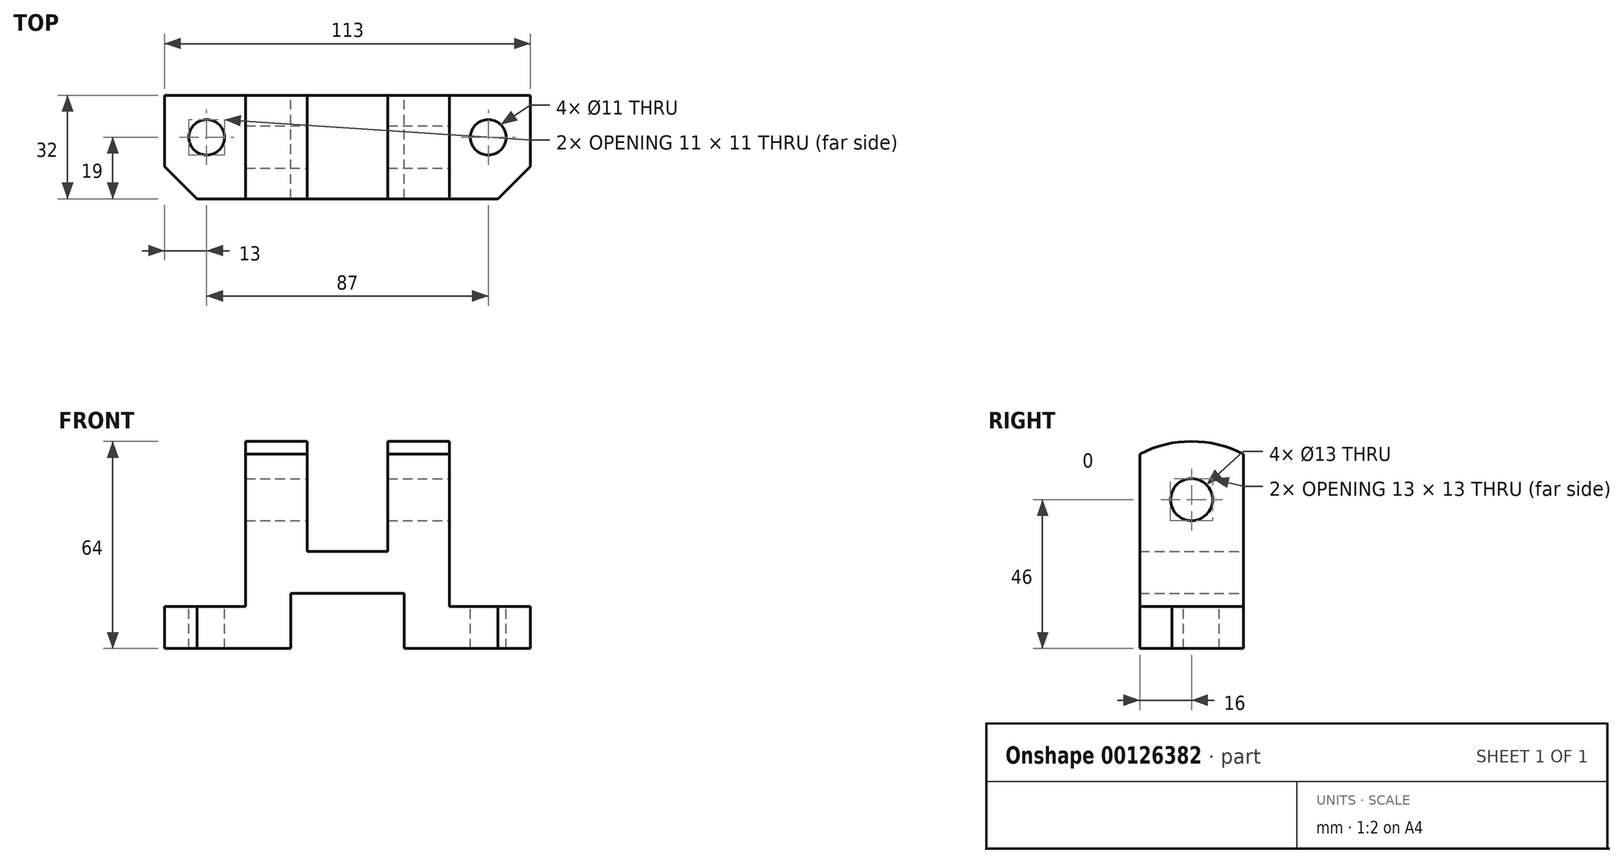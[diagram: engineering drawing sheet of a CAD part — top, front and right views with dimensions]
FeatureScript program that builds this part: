
annotation { "Feature Type Name" : "Feature", "Feature Type Description" : "" }
export const myFeature = defineFeature(function(context is Context, id is Id, definition is map)
    precondition{}
    {
        {
            var Q0;
            Q0=qCreatedBy(makeId("Front.planeOp"),FACE);
            var sketch = newSketch(context, id + "F0", { "sketchPlane" : qUnion([Q0])});
            skLineSegment(sketch, "E0", {"start": v(0, 0) * mm, "end": v(0, 13) * mm});
            skLineSegment(sketch, "E1", {"start": v(0, 13) * mm, "end": v(25, 13) * mm});
            skLineSegment(sketch, "E2", {"start": v(25, 13) * mm, "end": v(25, 64) * mm});
            skLineSegment(sketch, "E3", {"start": v(25, 64) * mm, "end": v(44, 64) * mm});
            skLineSegment(sketch, "E4", {"start": v(44, 64) * mm, "end": v(44, 30) * mm});
            skLineSegment(sketch, "E5", {"start": v(44, 30) * mm, "end": v(69, 30) * mm});
            skLineSegment(sketch, "E6", {"start": v(69, 30) * mm, "end": v(69, 64) * mm});
            skLineSegment(sketch, "E7", {"start": v(69, 64) * mm, "end": v(88, 64) * mm});
            skLineSegment(sketch, "E8", {"start": v(88, 64) * mm, "end": v(88, 13) * mm});
            skLineSegment(sketch, "E9", {"start": v(88, 13) * mm, "end": v(113, 13) * mm});
            skLineSegment(sketch, "E10", {"start": v(113, 13) * mm, "end": v(113, 0) * mm});
            skLineSegment(sketch, "E11", {"start": v(113, 0) * mm, "end": v(74, 0) * mm});
            skLineSegment(sketch, "E12", {"start": v(74, 0) * mm, "end": v(74, 17) * mm});
            skLineSegment(sketch, "E13", {"start": v(74, 17) * mm, "end": v(39, 17) * mm});
            skLineSegment(sketch, "E14", {"start": v(39, 17) * mm, "end": v(39, 0) * mm});
            skLineSegment(sketch, "E15", {"start": v(39, 0) * mm, "end": v(0, 0) * mm});
            skSolve(sketch);
        }
        {
            var Q0;
            Q0=makeQuery(id+"F0.imprint","IMPRINT",FACE,{"disambiguationData":[TD([[makeQuery(id+"F0.imprint","IMPRINT",EDGE,{"derivedFrom":sQuery(id+"F0.wireOp",EDGE,"E0")}),-1.0]])]});
            extrude(context, id + "F1", {"entities" : qUnion([Q0]), "endBound" : BoundingType.SYMMETRIC, "depth" : 32 * mm});
        }
        {
            var Q0;
            Q0=makeQuery(id+"F1.opExtrude","SWEPT_FACE",FACE,{"disambiguationData":[OSD([sQuery(id+"F0.wireOp",EDGE,"E8")])]});
            var sketch = newSketch(context, id + "F2", { "sketchPlane" : qUnion([Q0])});
            skLineSegment(sketch, "E16.0", {"start": v(-16, 64) * mm, "end": v(-16, 13) * mm});
            skLineSegment(sketch, "E16.1", {"start": v(16, 64) * mm, "end": v(16, 13) * mm});
            skArc(sketch, "E17", {"start": v(16, 60.13) * mm, "mid": v(0, 64) * mm, "end": v(-16, 60.13) * mm});
            skLineSegment(sketch, "E18.0", {"start": v(-16, 64) * mm, "end": v(16, 64) * mm});
            skCircle(sketch, "E19", {"center": v(0, 46) * mm, "radius": 6.5 * mm});
            skLineSegment(sketch, "E20", {"start": v(0, -19.5) * mm, "end": v(0, 83.55) * mm, "construction": true});
            skSolve(sketch);
        }
        {
            var Q0;
            Q0=makeQuery(id+"F2.imprint","IMPRINT",FACE,{"disambiguationData":[TD([[makeQuery(id+"F2.imprint","IMPRINT",EDGE,{"derivedFrom":sQuery(id+"F2.wireOp",EDGE,"E19")}),1.0]])]});
            extrude(context, id + "F3", {"entities" : qUnion([Q0]), "operationType" : NewBodyOperationType.REMOVE, "endBound" : BoundingType.THROUGH_ALL, "oppositeDirection" : true, "depth" : 25 * mm});
        }
        {
            var Q0;
            {var subQ0=sQuery(id+"F2.wireOp",EDGE,"E18.0");var subQ1=sQuery(id+"F2.wireOp",EDGE,"E16.1");var subQ2=makeQuery(id+"F2.imprint","INTERSECT",VERTEX,{"derivedFrom":[subQ1,subQ0]});Q0=makeQuery(id+"F2.imprint","IMPRINT",FACE,{"disambiguationData":[TD([[makeQuery(id+"F2.imprint","IMPRINT",EDGE,{"disambiguationData":[TD([[subQ2,-1.0]])],"derivedFrom":subQ1}),-1.0]])]});}
            var Q1;
            {var subQ0=sQuery(id+"F2.wireOp",EDGE,"E18.0");var subQ1=sQuery(id+"F2.wireOp",EDGE,"E16.0");var subQ2=makeQuery(id+"F2.imprint","INTERSECT",VERTEX,{"derivedFrom":[subQ1,subQ0]});Q1=makeQuery(id+"F2.imprint","IMPRINT",FACE,{"disambiguationData":[TD([[makeQuery(id+"F2.imprint","IMPRINT",EDGE,{"disambiguationData":[TD([[subQ2,-1.0]])],"derivedFrom":subQ1}),1.0]])]});}
            extrude(context, id + "F4", {"entities" : qUnion([Q0, Q1]), "operationType" : NewBodyOperationType.REMOVE, "endBound" : BoundingType.THROUGH_ALL, "oppositeDirection" : true, "depth" : 25 * mm});
        }
        {
            var Q0;
            Q0=makeQuery(id+"F1.opExtrude","SWEPT_FACE",FACE,{"disambiguationData":[OSD([sQuery(id+"F0.wireOp",EDGE,"E9")])]});
            var sketch = newSketch(context, id + "F5", { "sketchPlane" : qUnion([Q0])});
            skLineSegment(sketch, "E21.0", {"start": v(88, -16) * mm, "end": v(113, -16) * mm});
            skLineSegment(sketch, "E21.1", {"start": v(113, -16) * mm, "end": v(113, 16) * mm});
            skLineSegment(sketch, "E22", {"start": v(103, -16) * mm, "end": v(113, -6) * mm});
            skCircle(sketch, "E23", {"center": v(100, 3) * mm, "radius": 5.5 * mm});
            skLineSegment(sketch, "E24", {"start": v(103, -16) * mm, "end": v(113, -16) * mm});
            skLineSegment(sketch, "E25", {"start": v(113, -16) * mm, "end": v(113, -6) * mm});
            skSolve(sketch);
        }
        {
            var Q0;
            Q0=makeQuery(id+"F5.imprint","IMPRINT",FACE,{"disambiguationData":[TD([[makeQuery(id+"F5.imprint","IMPRINT",EDGE,{"derivedFrom":sQuery(id+"F5.wireOp",EDGE,"E23")}),1.0]])]});
            extrude(context, id + "F6", {"entities" : qUnion([Q0]), "operationType" : NewBodyOperationType.REMOVE, "endBound" : BoundingType.THROUGH_ALL, "oppositeDirection" : true, "depth" : 25 * mm});
        }
        {
            var Q0;
            Q0=makeQuery(id+"F5.imprint","IMPRINT",FACE,{"disambiguationData":[TD([[makeQuery(id+"F5.imprint","IMPRINT",EDGE,{"derivedFrom":sQuery(id+"F5.wireOp",EDGE,"E22")}),-1.0]])]});
            extrude(context, id + "F7", {"entities" : qUnion([Q0]), "operationType" : NewBodyOperationType.REMOVE, "endBound" : BoundingType.THROUGH_ALL, "oppositeDirection" : true, "depth" : 25 * mm});
        }
        {
            var Q0;
            Q0=makeQuery(id+"F1.opExtrude","SWEPT_FACE",FACE,{"disambiguationData":[OSD([sQuery(id+"F0.wireOp",EDGE,"E1")])]});
            var sketch = newSketch(context, id + "F8", { "sketchPlane" : qUnion([Q0])});
            skCircle(sketch, "E26", {"center": v(13, 3) * mm, "radius": 5.5 * mm});
            skLineSegment(sketch, "E27.0", {"start": v(0, -16) * mm, "end": v(25, -16) * mm});
            skLineSegment(sketch, "E27.1", {"start": v(0, -16) * mm, "end": v(0, 16) * mm});
            skLineSegment(sketch, "E28", {"start": v(0, -6) * mm, "end": v(10, -16) * mm});
            skLineSegment(sketch, "E29", {"start": v(0, -6) * mm, "end": v(0, -16) * mm});
            skLineSegment(sketch, "E30", {"start": v(0, -16) * mm, "end": v(10, -16) * mm});
            skSolve(sketch);
        }
        {
            var Q0;
            Q0=makeQuery(id+"F8.imprint","IMPRINT",FACE,{"disambiguationData":[TD([[makeQuery(id+"F8.imprint","IMPRINT",EDGE,{"derivedFrom":sQuery(id+"F8.wireOp",EDGE,"E26")}),1.0]])]});
            extrude(context, id + "F9", {"entities" : qUnion([Q0]), "operationType" : NewBodyOperationType.REMOVE, "endBound" : BoundingType.THROUGH_ALL, "oppositeDirection" : true, "depth" : 25 * mm});
        }
        {
            var Q0;
            Q0=makeQuery(id+"F8.imprint","IMPRINT",FACE,{"disambiguationData":[TD([[makeQuery(id+"F8.imprint","IMPRINT",EDGE,{"derivedFrom":sQuery(id+"F8.wireOp",EDGE,"E28")}),-1.0]])]});
            extrude(context, id + "F10", {"entities" : qUnion([Q0]), "operationType" : NewBodyOperationType.REMOVE, "endBound" : BoundingType.THROUGH_ALL, "oppositeDirection" : true, "depth" : 25 * mm});
        }
    });
